# Revit family: TH6016661_Kit por 6 Accesorios Thames(Jabonera)
name_source: partatom
category: Plumbing Fixtures
units: mm (PartAtom-declared; Revit-internal decimal feet)

## family parameters
Always vertical = Yes
Cut with Voids When Loaded = No
OmniClass Number = 23.19.25.13.21.17
OmniClass Title = Fittings
Part Type = Normal
Room Calculation Point = No
Round Connector Dimension = Use Diameter
Shared = No
Work Plane-Based = No

## types (1)
- TH6016661_Kit por 6 Accesorios Thames(Jabonera)
    Acabado = Cromado
    Colección = Gama Media 2010
    Componentes = Percha, Toallero, Jabonera, Barra, Cepillera, Portarrollo
    Creado por = IDD
    Description = Nuestro kit de accesorios que reflejan las últimas tendencias de diseño, convirtiéndose así en el mejor complemento para tu baño. ¡Pídelo ahora!
    Fecha de creación = 19/08/2020
    Garantía = 30 años en estructura
    Garantías de otros componentes = 2 años en acabados
    Línea = Torino
    Material = Corona_Cromo
    Materiales = Cromado
    Número de piezas = 6
    Resistencia = Resistente a la corrosión pelado y decoloración por agua, Resistencia al peso general hasta 9 kg, Resistencia al peso del toallero barra hasta 23 kg
    URL = https://corona.co
    Uso = Residencial

## geometry (parser evidence)
native form markers: Sweep x3
no freeform markers — native parametric forms only
